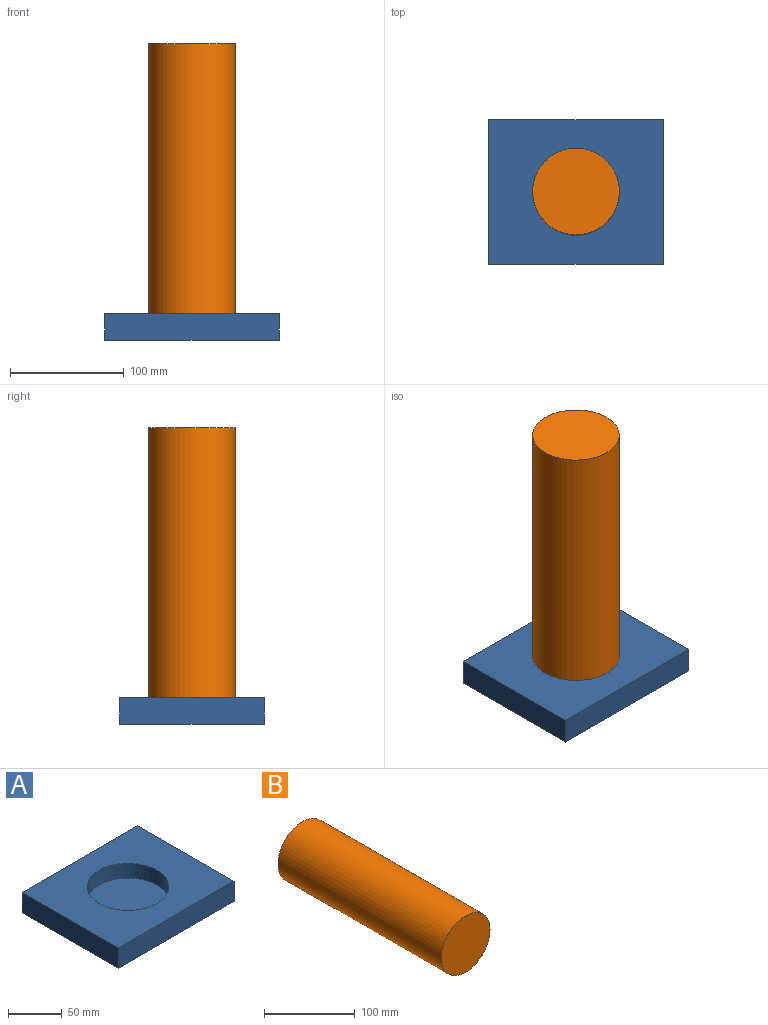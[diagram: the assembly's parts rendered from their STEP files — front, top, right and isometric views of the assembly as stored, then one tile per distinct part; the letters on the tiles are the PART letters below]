
ASSEMBLY  parts=2 mates=1
PART A: 8 faces, bbox 152.9x126.9x23.2 mm
  f0: plane 126.91x23.2mm, normal (1,0,0), area 2944.3mm2, adj f1,f3,f4,f5
  f1: plane 152.87x126.91mm, normal (0,0,1), area 14840.4mm2, adj f0,f2,f4,f5,f6
  f2: plane 126.91x23.2mm, normal (-1,0,0), area 2944.3mm2, adj f1,f3,f4,f5
  f3: plane 152.87x126.91mm, normal (0,0,-1), area 19400.8mm2, adj f0,f2,f4,f5
  f4: plane 152.87x23.2mm, normal (0,-1,0), area 3546.8mm2, adj f0,f1,f2,f3
  f5: plane 152.87x23.2mm, normal (0,1,0), area 3546.8mm2, adj f0,f1,f2,f3
  f6: cylinder r=38.1mm len=76.2mm, axis (0,0,1), area 4047.4mm2, adj f1,f7
  f7: plane 76.2x76.2mm, normal (0,0,1), area 4560.4mm2, adj f6
PART B: 3 faces, bbox 76.2x254x76.2 mm
  f0: cylinder r=38.1mm len=254mm, axis (0,1,0), area 60804.9mm2, adj f1,f2
  f1: plane 76.2x76.2mm, normal (0,-1,0), area 4560.4mm2, adj f0
  f2: plane 76.2x76.2mm, normal (0,1,0), area 4560.4mm2, adj f0
PLACE A t=(-23.4,105.29,0)mm
PLACE B rot(axis=(-1,0,0),90deg) t=(-23.4,105.29,121.69)mm
MATE fastened B.f0 <-> A.f6  axis (0,0,-1) through (-23.4,105.29,-5.31)mm
